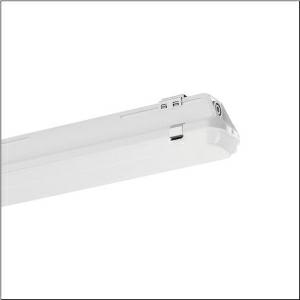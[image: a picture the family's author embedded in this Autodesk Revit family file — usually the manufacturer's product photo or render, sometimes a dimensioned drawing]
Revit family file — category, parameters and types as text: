
# Revit family: monsun_21_parking_51fg20dl430k
name_source: partatom
category: Lighting Fixtures
units: mm (PartAtom-declared; Revit-internal decimal feet)

## family parameters
Cut with Voids When Loaded = No
Host = Face
Light Source = No
Part Type = Normal
Room Calculation Point = No
Round Connector Dimension = Use Diameter
Shared = No

## types (1)
- --- (1 x LED, 3850 lm, 24 W, 4000K)
    Apparent Load = 24 VA
    CIE Flux Codes = 45 75 93 94 100
    Color Rendering = 80
    Color Temperature = 4000K
    Default Elevation = 1800 mm
    Description = Monsun 21 parking, damp-proof luminaire, chain hanger, primary optical cover: enclosure, of PC, light emission: direct distribution, primary light characteristic: symmetric, installation type: suspended mounting, surface-mounted, horizontal mounting, vertical mounting, LED, rated luminous flux: 3.850lm, luminous efficacy: 160lm/W, light colour: 840, colour temperature: 4000K, control gear: DALI 2, with terminal, 5-pole, max. 2.5mm², mains connection: 220..240V, AC, 50/60Hz, rated input power: 24W, housing, of glass-fibre reinforced plastic, uncoated, bright grey, incl. chain hanger, length: 1.299mm, width: 90mm, height: 88mm, clip for enclosure, of stainless steel (V2A), ceiling mounting element, of stainless steel (V2A), chain hanger, of stainless steel (V2A), protection rating (complete): IP66, insulation class (complete): insulation class I (protective earthing), certification: CE, ENEC, VDE, UKCA, protection symbol: D, impact resistance: IK08, permissible operating ambient temperature: -25..+35°C, standard: EN 50419, EN 60598-2-1, corresponds to IFS (International Featured Standards) requirements for safety and quality in the food industry, for indoor or canopied outdoor use, no direct snow, no direct sun, no direct rain, LABS conformity tested according to VDMA 24364:2018-05, contact your sales advisor before using the luminaires in applications with unclear chemical exposure, large temperature fluctuations or condensation-forming humidity, packaging unit: 1 piece
    Height = 88 mm
    Lamp = 1 x LED
    Lamp Light Flux = 3850 lm
    Lamp Power = 24 W
    Lamp count = 1
    Length = 1299 mm
    Luminous efficacy = 160 lm/W
    Manufacturer = Siteco
    ModVariant = No
    Model = 51FG20DL430K
    Mounting Place = Ceiling
    Mounting Type = Surface mounted
    Number of Poles = 1
    OnlyDefault = Yes
    Power Factor = 1
    Product Name = Monsun 21 parking
    Product group = damp-proof luminaire
    ProductGroupID = 300
    Protection Class = Protection class I
    Protection Degree = IP 66
    RLX_Detail_Level = 1
    RLX_Emergency_Light_Flux = 0 lm
    RLX_Emergency_Type = 0
    RLX_Emergency_Type_DB = No
    RlxData = <blob elided: 93297 chars, md5=30185361>
    Socket = socket
    Standby Power = 0 W
    System Light Flux = 3850 lm
    System Power = 24 W
    Type Comments = factory setting: luminous flux: 100 % | dim-lin: 254 | 161 mA
    Type Image = l_1319656.jpg
    URL = http://relux.com
    VarID = @adj_037221
    Voltage = 0 V
    Weight = 0.00 kg
    Width = 90 mm

## geometry (parser evidence)
native form markers: Blend x4, Sweep x12
no freeform markers — native parametric forms only
